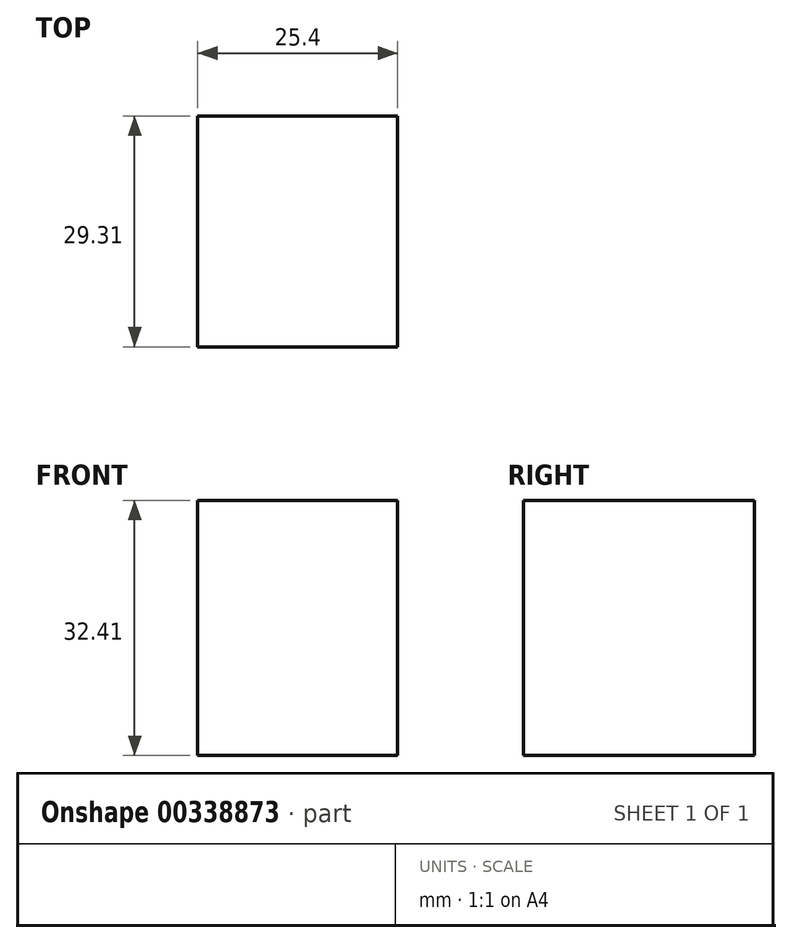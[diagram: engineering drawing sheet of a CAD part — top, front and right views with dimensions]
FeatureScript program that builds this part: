
annotation { "Feature Type Name" : "Feature", "Feature Type Description" : "" }
export const myFeature = defineFeature(function(context is Context, id is Id, definition is map)
    precondition{}
    {
        {
            var Q0;
            Q0=qCreatedBy(makeId("Right.planeOp"),FACE);
            var sketch = newSketch(context, id + "F0", { "sketchPlane" : qUnion([Q0])});
            skLineSegment(sketch, "E0.bottom", {"start": v(0, 32.41) * mm, "end": v(29.3, 32.41) * mm});
            skLineSegment(sketch, "E0.top", {"start": v(0, 0) * mm, "end": v(29.3, 0) * mm});
            skLineSegment(sketch, "E0.left", {"start": v(0, 32.41) * mm, "end": v(0, 0) * mm});
            skLineSegment(sketch, "E0.right", {"start": v(29.3, 32.41) * mm, "end": v(29.3, 0) * mm});
            skSolve(sketch);
        }
        {
            var Q0;
            Q0=sQuery(id+"F0.wireOp",EDGE,"E0.left");
            var Q1;
            Q1=sQuery(id+"F0.wireOp",EDGE,"E0.bottom");
            var Q2;
            Q2=sQuery(id+"F0.wireOp",EDGE,"E0.right");
            var Q3;
            Q3=sQuery(id+"F0.wireOp",EDGE,"E0.top");
            extrude(context, id + "F1", {"bodyType" : ToolBodyType.SURFACE, "surfaceEntities" : qUnion([Q0, Q1, Q2, Q3]), "depth" : 25.4 * mm});
        }
    });
